# Revit family: Furniture-Floor_Mount-Vanity-KOHLER-PASTORIFE-K-98989T_1
name_source: partatom
category: Plumbing Fixtures
revit_build: Autodesk Revit 2017 (Build: 20160225_1515(x64)
units: mm (PartAtom-declared; Revit-internal decimal feet)

## family parameters
Cut with Voids When Loaded = No
Host = Face
OmniClass Number = 23.31.13.00
OmniClass Title = Sinks
Part Type = Normal
Room Calculation Point = No
Round Connector Dimension = Use Diameter
Shared = No

## types (1)
- F02- Light Wheat Yellow
    ADA Compliant = No
    Assembly Code = D2010400
    CW Connection = No
    Cold Water Inlet = Cold Water Inlet
    Date Modified = 03/07/2021
    Default Elevation = 0"
    Description = PASTORIFE 1490 MM SET W/ARCHER LAV 1
    Drain Included = No
    Finish = Kohler-Wood-F02-Light_Wheat _Yellow
    HW Connection = No
    Hardware Included = Yes
    Height = 33 1/16"
    Hot Water Inlet = Hot Water Inlet
    Length = 24"
    Manufacturer = KOHLER Co.
    Master Format 2014 = 22 41 16
    Master Format 2014 Name = Residential Lavatories and Sinks
    Material = Solid Wood Construction
    Model = K-98989T-1-F02
    Product Name = PASTORIFE
    Type = 1
    URL = http://www.kohler.com.cn
    Vent Connection = No
    Waste Connection = Yes
    Waste Water Outlet 1 = Waste Water Outlet 1
    Waste Water Outlet 2 = Waste Water Outlet 2
    WaterSense Certified = No
    Width = 58 11/16"

## geometry (parser evidence)
native form markers: Sweep x3
no freeform markers — native parametric forms only
